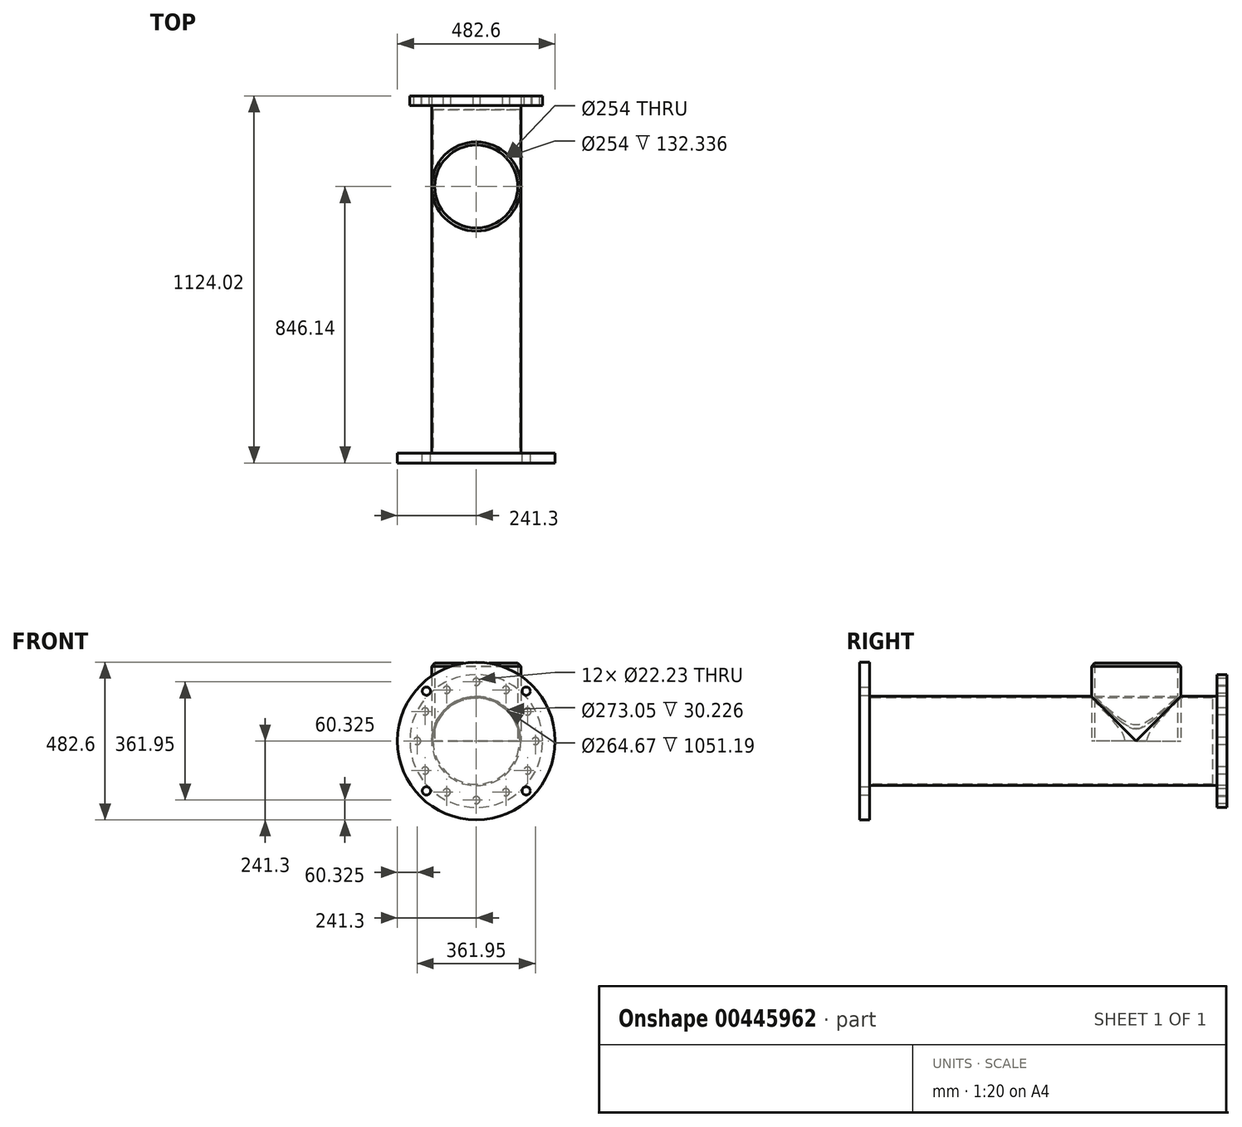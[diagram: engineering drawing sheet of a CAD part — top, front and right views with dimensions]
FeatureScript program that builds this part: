
annotation { "Feature Type Name" : "Feature", "Feature Type Description" : "" }
export const myFeature = defineFeature(function(context is Context, id is Id, definition is map)
    precondition{}
    {
        {
            var Q0;
            Q0=qCreatedBy(makeId("Front.planeOp"),FACE);
            var sketch = newSketch(context, id + "F0", { "sketchPlane" : qUnion([Q0])});
            skCircle(sketch, "E0", {"center": v(0, 0) * mm, "radius": 136.53 * mm});
            skSolve(sketch);
        }
        {
            var Q0;
            Q0=makeQuery(id+"F0.imprint","IMPRINT",FACE,{"disambiguationData":[TD([[makeQuery(id+"F0.imprint","IMPRINT",EDGE,{"derivedFrom":sQuery(id+"F0.wireOp",EDGE,"E0")}),1.0]])]});
            var Q1;
            Q1=sQuery(id+"F0.wireOp",EDGE,"E0");
            extrude(context, id + "F1", {"entities" : qUnion([Q0]), "surfaceEntities" : qUnion([Q1]), "depth" : 1063.56 * mm});
        }
        {
            var Q0;
            Q0=makeQuery(id+"F1.opExtrude","CAP_FACE",FACE,{"disambiguationData":[OSD([sQuery(id+"F0.wireOp",EDGE,"E0")])],"isStart":false});
            var sketch = newSketch(context, id + "F2", { "sketchPlane" : qUnion([Q0])});
            skCircle(sketch, "E1", {"center": v(0, 0) * mm, "radius": 132.33 * mm});
            skSolve(sketch);
        }
        {
            var Q0;
            Q0=makeQuery(id+"F2.imprint","IMPRINT",FACE,{"disambiguationData":[TD([[makeQuery(id+"F2.imprint","IMPRINT",EDGE,{"derivedFrom":sQuery(id+"F2.wireOp",EDGE,"E1")}),1.0]])]});
            extrude(context, id + "F3", {"entities" : qUnion([Q0]), "operationType" : NewBodyOperationType.REMOVE, "oppositeDirection" : true, "depth" : 1051.2 * mm, "offsetDistance" : 25.4 * mm});
        }
        {
            var Q0;
            Q0=makeQuery(id+"F1.opExtrude","CAP_FACE",FACE,{"disambiguationData":[OSD([sQuery(id+"F0.wireOp",EDGE,"E0")])],"isStart":false});
            var sketch = newSketch(context, id + "F4", { "sketchPlane" : qUnion([Q0])});
            skCircle(sketch, "E2", {"center": v(0, 0) * mm, "radius": 241.3 * mm});
            skCircle(sketch, "E3", {"center": v(152.66, 152.66) * mm, "radius": 12.7 * mm});
            skCircle(sketch, "E4", {"center": v(-152.66, 152.66) * mm, "radius": 12.7 * mm});
            skCircle(sketch, "E5", {"center": v(152.66, -152.66) * mm, "radius": 12.7 * mm});
            skCircle(sketch, "E6", {"center": v(-152.66, -152.66) * mm, "radius": 12.7 * mm});
            skSolve(sketch);
        }
        {
            var Q0;
            Q0 = qSketchRegion(id + "F4", true);
            extrude(context, id + "F5", {"entities" : qUnion([Q0]), "operationType" : NewBodyOperationType.ADD, "depth" : 30.23 * mm, "offsetDistance" : 25.4 * mm});
        }
        {
            var Q0;
            Q0=makeQuery(id+"F1.opExtrude","CAP_FACE",FACE,{"disambiguationData":[OSD([sQuery(id+"F0.wireOp",EDGE,"E0")])],"isStart":true});
            var sketch = newSketch(context, id + "F6", { "sketchPlane" : qUnion([Q0])});
            skCircle(sketch, "E7", {"center": v(0, 0) * mm, "radius": 203.2 * mm});
            skCircle(sketch, "E8", {"center": v(-156.73, 90.49) * mm, "radius": 11.11 * mm});
            skCircle(sketch, "E9", {"center": v(-90.49, 156.73) * mm, "radius": 11.11 * mm});
            skCircle(sketch, "E10", {"center": v(0, 180.98) * mm, "radius": 11.11 * mm});
            skCircle(sketch, "E11.MirrorC", {"center": v(156.73, 90.49) * mm, "radius": 11.11 * mm});
            skCircle(sketch, "E12.MirrorC", {"center": v(90.49, 156.73) * mm, "radius": 11.11 * mm});
            skCircle(sketch, "E13.MirrorC", {"center": v(156.73, -90.49) * mm, "radius": 11.11 * mm});
            skCircle(sketch, "E14.MirrorC", {"center": v(90.49, -156.73) * mm, "radius": 11.11 * mm});
            skCircle(sketch, "E15.MirrorC", {"center": v(0, -180.98) * mm, "radius": 11.11 * mm});
            skCircle(sketch, "E16.MirrorC", {"center": v(-90.49, -156.73) * mm, "radius": 11.11 * mm});
            skCircle(sketch, "E17.MirrorC", {"center": v(-156.73, -90.49) * mm, "radius": 11.11 * mm});
            skCircle(sketch, "E18", {"center": v(-180.98, 0) * mm, "radius": 11.11 * mm});
            skCircle(sketch, "E19", {"center": v(180.98, 0) * mm, "radius": 11.11 * mm});
            skCircle(sketch, "E20", {"center": v(0, 0) * mm, "radius": 127 * mm});
            skSolve(sketch);
        }
        {
            var Q0;
            Q0=makeQuery(id+"F6.imprint","IMPRINT",FACE,{"disambiguationData":[TD([[makeQuery(id+"F6.imprint","IMPRINT",EDGE,{"derivedFrom":sQuery(id+"F6.wireOp",EDGE,"E7")}),1.0]])]});
            extrude(context, id + "F7", {"entities" : qUnion([Q0]), "depth" : 30.23 * mm, "offsetDistance" : 25.4 * mm});
        }
        {
            var Q0;
            Q0=qCreatedBy(makeId("Top.planeOp"),FACE);
            var sketch = newSketch(context, id + "F8", { "sketchPlane" : qUnion([Q0])});
            skCircle(sketch, "E21", {"center": v(0, -247.65) * mm, "radius": 136.53 * mm});
            skCircle(sketch, "E22", {"center": v(0, -247.65) * mm, "radius": 127 * mm});
            skSolve(sketch);
        }
        {
            var Q0;
            Q0 = qSketchRegion(id + "F8", true);
            extrude(context, id + "F9", {"entities" : qUnion([Q0]), "operationType" : NewBodyOperationType.ADD, "depth" : 238.12 * mm, "offsetDistance" : 25.4 * mm});
        }
        {
            var Q0;
            Q0=makeQuery(id+"F9.opExtrude","CAP_EDGE",EDGE,{"disambiguationData":[OSD([sQuery(id+"F8.wireOp",EDGE,"E21")])],"isStart":false});
            chamfer(context, id + "F10", {"entities" : qUnion([Q0]), "width" : 9.52 * mm, "tangentPropagation" : true});
        }
        {
            var Q0;
            Q0=qCreatedBy(makeId("Top.planeOp"),FACE);
            var sketch = newSketch(context, id + "F11", { "sketchPlane" : qUnion([Q0])});
            skCircle(sketch, "E23", {"center": v(0, -247.65) * mm, "radius": 127 * mm});
            skSolve(sketch);
        }
        {
            var Q0;
            Q0 = qSketchRegion(id + "F11", true);
            var Q1;
            Q1=sQuery(id+"F11.wireOp",EDGE,"E23");
            extrude(context, id + "F12", {"entities" : qUnion([Q0]), "operationType" : NewBodyOperationType.REMOVE, "surfaceEntities" : qUnion([Q1]), "oppositeDirection" : true, "depth" : 25.4 * mm, "offsetDistance" : 25.4 * mm});
        }
    });
